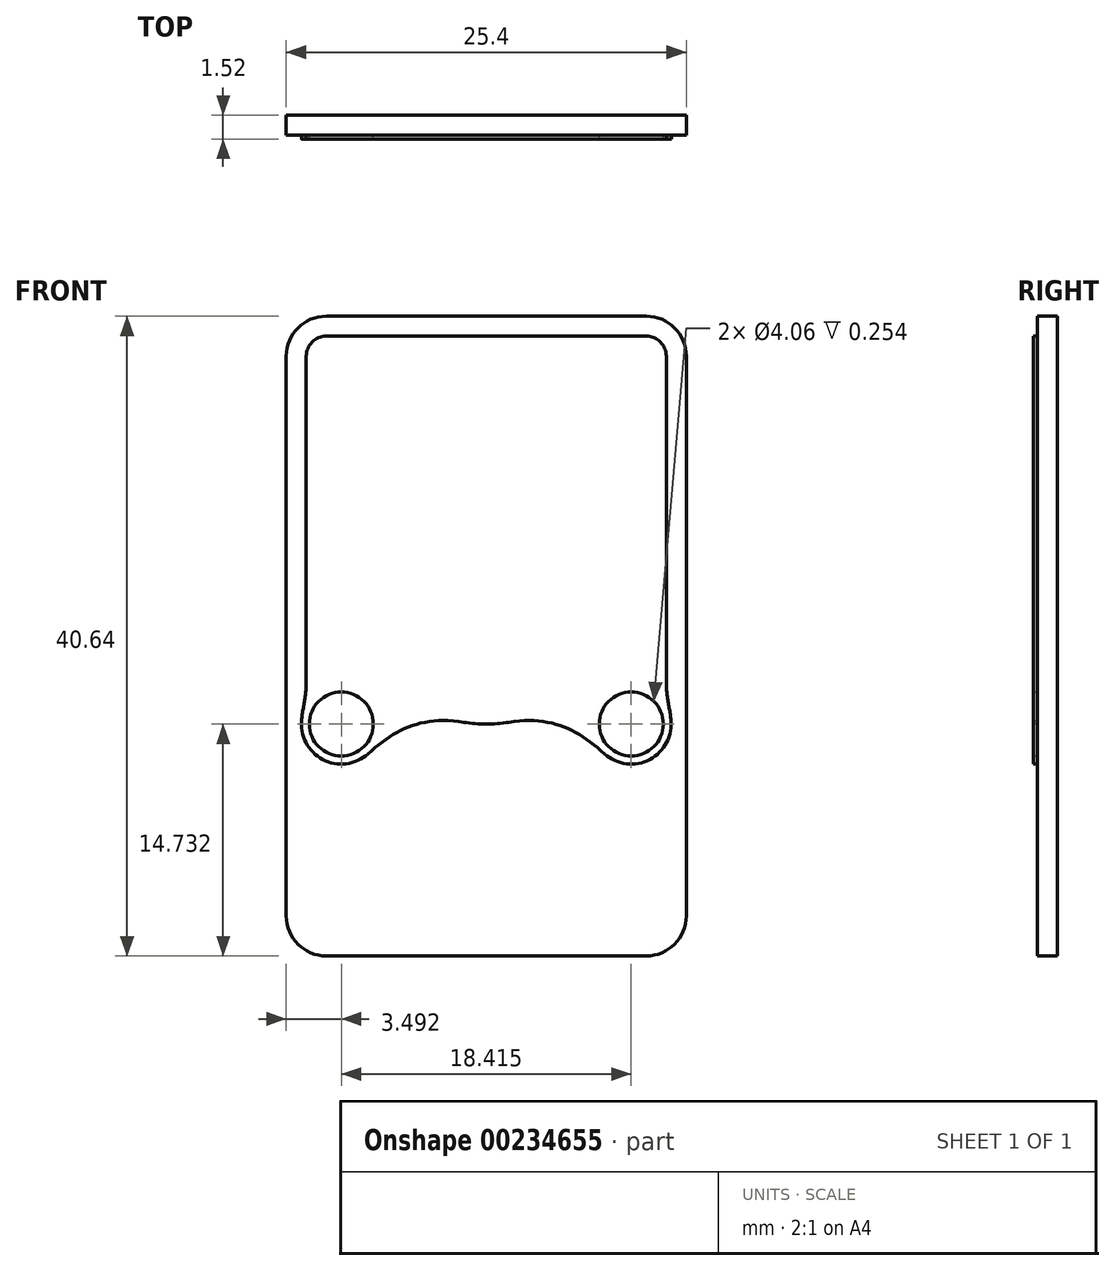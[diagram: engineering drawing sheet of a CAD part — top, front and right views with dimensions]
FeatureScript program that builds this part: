
annotation { "Feature Type Name" : "Feature", "Feature Type Description" : "" }
export const myFeature = defineFeature(function(context is Context, id is Id, definition is map)
    precondition{}
    {
        {
            var Q0;
            Q0=qCreatedBy(makeId("Front.planeOp"),FACE);
            var sketch = newSketch(context, id + "F0", { "sketchPlane" : qUnion([Q0])});
            skLineSegment(sketch, "E0.bottom", {"start": v(12.7, 20.32) * mm, "end": v(-12.7, 20.32) * mm});
            skLineSegment(sketch, "E0.top", {"start": v(12.7, -20.32) * mm, "end": v(-12.7, -20.32) * mm});
            skLineSegment(sketch, "E0.left", {"start": v(12.7, 20.32) * mm, "end": v(12.7, -20.32) * mm});
            skLineSegment(sketch, "E0.right", {"start": v(-12.7, 20.32) * mm, "end": v(-12.7, -20.32) * mm});
            skPoint(sketch, "E0.middle", {"position": v(0, 0) * mm});
            skSolve(sketch);
        }
        {
            var Q0;
            Q0 = qSketchRegion(id + "F0", true);
            extrude(context, id + "F1", {"entities" : qUnion([Q0]), "depth" : 1.27 * mm});
        }
        {
            var Q0;
            Q0=makeQuery(id+"F1.opExtrude","CAP_FACE",FACE,{"disambiguationData":[OSD([sQuery(id+"F0.wireOp",EDGE,"E0.bottom"),sQuery(id+"F0.wireOp",EDGE,"E0.top"),sQuery(id+"F0.wireOp",EDGE,"E0.left"),sQuery(id+"F0.wireOp",EDGE,"E0.right")])],"isStart":false});
            var sketch = newSketch(context, id + "F2", { "sketchPlane" : qUnion([Q0])});
            skLineSegment(sketch, "E1", {"start": v(0, 20.32) * mm, "end": v(0, -20.32) * mm, "construction": true});
            skLineSegment(sketch, "E2", {"start": v(0, -20.32) * mm, "end": v(12.7, 0) * mm, "construction": true});
            skLineSegment(sketch, "E3", {"start": v(12.7, 0) * mm, "end": v(-12.7, 0) * mm, "construction": true});
            skLineSegment(sketch, "E4", {"start": v(-12.7, 0) * mm, "end": v(0, -20.32) * mm, "construction": true});
            skLineSegment(sketch, "E5", {"start": v(-12.7, 0) * mm, "end": v(0, 20.32) * mm, "construction": true});
            skLineSegment(sketch, "E6", {"start": v(12.7, 0) * mm, "end": v(0, 20.32) * mm, "construction": true});
            skCircle(sketch, "E7", {"center": v(-9.2, -5.59) * mm, "radius": 2.54 * mm});
            skCircle(sketch, "E8.MirrorC", {"center": v(9.2, -5.59) * mm, "radius": 2.54 * mm});
            skEllipse(sketch, "E9", {"center": v(0, -2.8) * mm, "majorRadius": 5.08 * mm, "minorRadius": 2.8 * mm, "majorAxis": v(1, 0)});
            skLineSegment(sketch, "E10.bottom", {"start": v(11.43, 19.05) * mm, "end": v(-11.43, 19.05) * mm});
            skLineSegment(sketch, "E10.left", {"start": v(11.43, 19.05) * mm, "end": v(11.43, -2.94) * mm});
            skLineSegment(sketch, "E10.right", {"start": v(-11.43, 19.05) * mm, "end": v(-11.43, -2.94) * mm});
            skPoint(sketch, "E10.middle", {"position": v(0, 8.06) * mm});
            skFitSpline(sketch, "E11", {"points": [v(-11.43, -2.94) * mm, v(-11.73, -5.27) * mm], "startDerivative": vector(0, -2.34) * mm, "endDerivative": vector(-0.3, -2.33) * mm});
            skFitSpline(sketch, "E12", {"points": [v(-1.42, -5.48) * mm, v(-7.52, -7.48) * mm], "startDerivative": vector(-8.05, 1.29) * mm, "endDerivative": vector(-5.29, -4.71) * mm});
            skFitSpline(sketch, "E13.MirrorCS", {"points": [v(11.43, -2.94) * mm, v(11.73, -5.27) * mm], "startDerivative": vector(0, -2.34) * mm, "endDerivative": vector(0.3, -2.33) * mm});
            skFitSpline(sketch, "E14.MirrorCS", {"points": [v(1.42, -5.48) * mm, v(7.52, -7.48) * mm], "startDerivative": vector(8.05, 1.29) * mm, "endDerivative": vector(5.29, -4.71) * mm});
            skCircle(sketch, "E15.0", {"center": v(-9.2, -5.59) * mm, "radius": 2.03 * mm});
            skCircle(sketch, "E16.MirrorC", {"center": v(9.2, -5.59) * mm, "radius": 2.03 * mm});
            skEllipse(sketch, "E17.MirrorC", {"center": v(0, -2.8) * mm, "majorRadius": 5.08 * mm, "minorRadius": 2.8 * mm, "majorAxis": v(-1, 0)});
            skFitSpline(sketch, "E18.0", {"points": [v(-4.53, -2.43) * mm, v(-4.6, -2.8) * mm, v(-4.53, -3.16) * mm, v(-4.32, -3.56) * mm, v(-3.93, -3.96) * mm, v(-3.37, -4.33) * mm, v(-2.67, -4.65) * mm, v(-1.84, -4.9) * mm, v(-0.94, -5.05) * mm, v(0, -5.1) * mm, v(0.94, -5.05) * mm, v(1.84, -4.9) * mm, v(2.67, -4.65) * mm, v(3.37, -4.33) * mm, v(3.93, -3.96) * mm, v(4.32, -3.56) * mm, v(4.53, -3.16) * mm, v(4.6, -2.8) * mm, v(4.53, -2.43) * mm, v(4.32, -2.03) * mm, v(3.93, -1.63) * mm, v(3.37, -1.25) * mm, v(2.67, -0.94) * mm, v(1.84, -0.7) * mm, v(0.94, -0.54) * mm, v(0, -0.5) * mm, v(-0.94, -0.54) * mm, v(-1.84, -0.7) * mm, v(-2.67, -0.94) * mm, v(-3.37, -1.25) * mm, v(-3.93, -1.63) * mm, v(-4.32, -2.03) * mm, v(-4.53, -2.43) * mm, v(-4.6, -2.8) * mm, v(-4.53, -3.16) * mm, v(-4.53, -2.43) * mm]});
            skSolve(sketch);
        }
        {
            var Q0;
            Q0 = qSketchRegion(id + "F2", true);
            extrude(context, id + "F3", {"entities" : qUnion([Q0]), "operationType" : NewBodyOperationType.ADD, "depth" : 0.25 * mm});
        }
        {
            var Q0;
            Q0=makeQuery(id+"F1.opExtrude","SWEPT_EDGE",EDGE,{"disambiguationData":[OSD([sQuery(id+"F0.wireOp",EDGE,"E0.top"),sQuery(id+"F0.wireOp",EDGE,"E0.left")])]});
            var Q1;
            Q1=makeQuery(id+"F1.opExtrude","SWEPT_EDGE",EDGE,{"disambiguationData":[OSD([sQuery(id+"F0.wireOp",EDGE,"E0.top"),sQuery(id+"F0.wireOp",EDGE,"E0.right")])]});
            var Q2;
            Q2=makeQuery(id+"F1.opExtrude","SWEPT_EDGE",EDGE,{"disambiguationData":[OSD([sQuery(id+"F0.wireOp",EDGE,"E0.bottom"),sQuery(id+"F0.wireOp",EDGE,"E0.right")])]});
            var Q3;
            Q3=makeQuery(id+"F1.opExtrude","SWEPT_EDGE",EDGE,{"disambiguationData":[OSD([sQuery(id+"F0.wireOp",EDGE,"E0.bottom"),sQuery(id+"F0.wireOp",EDGE,"E0.left")])]});
            fillet(context, id + "F4", {"entities" : qUnion([Q0, Q1, Q2, Q3]), "radius" : 2.54 * mm, "tangentPropagation" : true, "allowEdgeOverflow" : false});
        }
        {
            var Q0;
            Q0=makeQuery(id+"F3.opExtrude","SWEPT_EDGE",EDGE,{"disambiguationData":[OSD([sQuery(id+"F2.wireOp",EDGE,"E10.bottom"),sQuery(id+"F2.wireOp",EDGE,"E10.right")])]});
            var Q1;
            Q1=makeQuery(id+"F3.opExtrude","SWEPT_EDGE",EDGE,{"disambiguationData":[OSD([sQuery(id+"F2.wireOp",EDGE,"E10.bottom"),sQuery(id+"F2.wireOp",EDGE,"E10.left")])]});
            fillet(context, id + "F5", {"entities" : qUnion([Q0, Q1]), "radius" : 1.27 * mm, "tangentPropagation" : true, "allowEdgeOverflow" : false});
        }
    });
